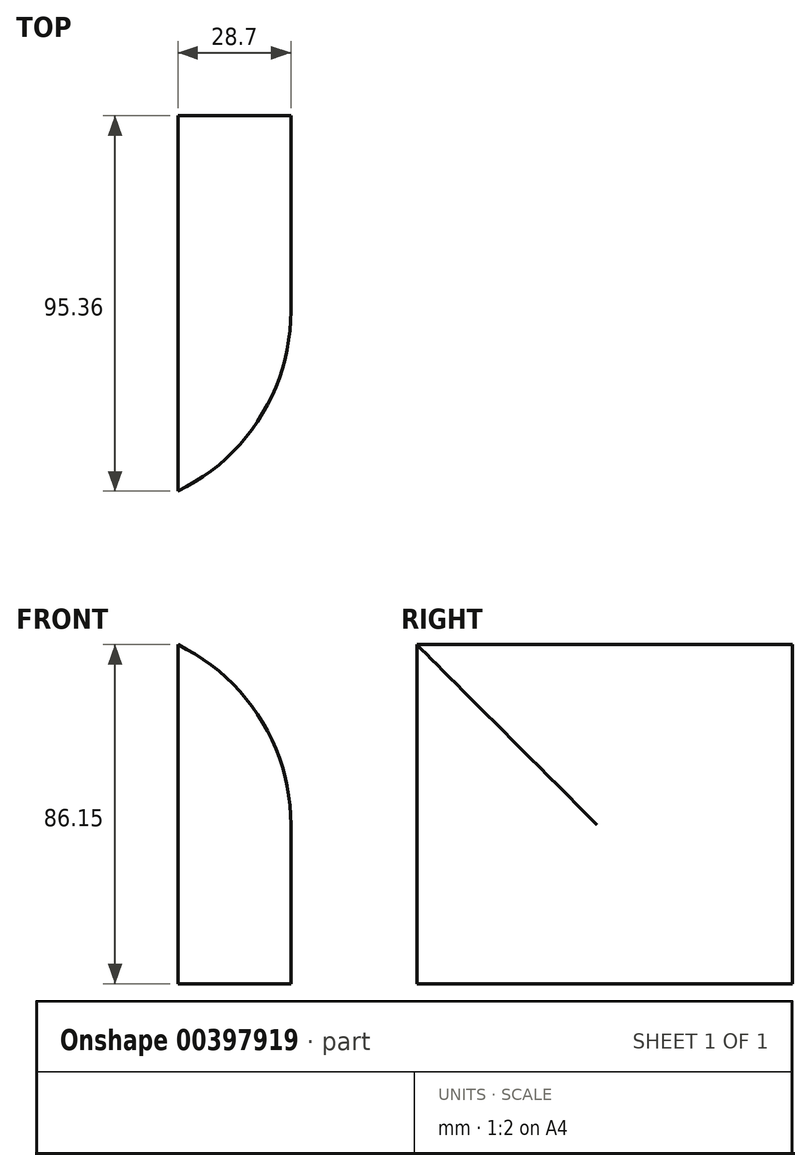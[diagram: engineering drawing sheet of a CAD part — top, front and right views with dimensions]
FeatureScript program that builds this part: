
annotation { "Feature Type Name" : "Feature", "Feature Type Description" : "" }
export const myFeature = defineFeature(function(context is Context, id is Id, definition is map)
    precondition{}
    {
        {
            var Q0;
            Q0=qCreatedBy(makeId("Right.planeOp"),FACE);
            var sketch = newSketch(context, id + "F0", { "sketchPlane" : qUnion([Q0])});
            skLineSegment(sketch, "E0.bottom", {"start": v(-180.95, 119.17) * mm, "end": v(-276.31, 119.17) * mm});
            skLineSegment(sketch, "E0.top", {"start": v(-180.95, 205.32) * mm, "end": v(-276.31, 205.32) * mm});
            skLineSegment(sketch, "E0.left", {"start": v(-180.95, 119.17) * mm, "end": v(-180.95, 205.32) * mm});
            skLineSegment(sketch, "E0.right", {"start": v(-276.31, 119.17) * mm, "end": v(-276.31, 205.32) * mm});
            skSolve(sketch);
        }
        {
            var Q0;
            Q0 = qSketchRegion(id + "F0", true);
            extrude(context, id + "F1", {"entities" : qUnion([Q0]), "depth" : 28.7 * mm});
        }
        {
            var Q0;
            Q0=makeQuery(id+"F1.opExtrude","CAP_EDGE",EDGE,{"disambiguationData":[OSD([sQuery(id+"F0.wireOp",EDGE,"E0.right")])],"isStart":false});
            var Q1;
            Q1=makeQuery(id+"F1.opExtrude","CAP_EDGE",EDGE,{"disambiguationData":[OSD([sQuery(id+"F0.wireOp",EDGE,"E0.top")])],"isStart":false});
            fillet(context, id + "F2", {"entities" : qUnion([Q0, Q1]), "radius" : 50.8 * mm, "tangentPropagation" : true, "allowEdgeOverflow" : false});
        }
    });
